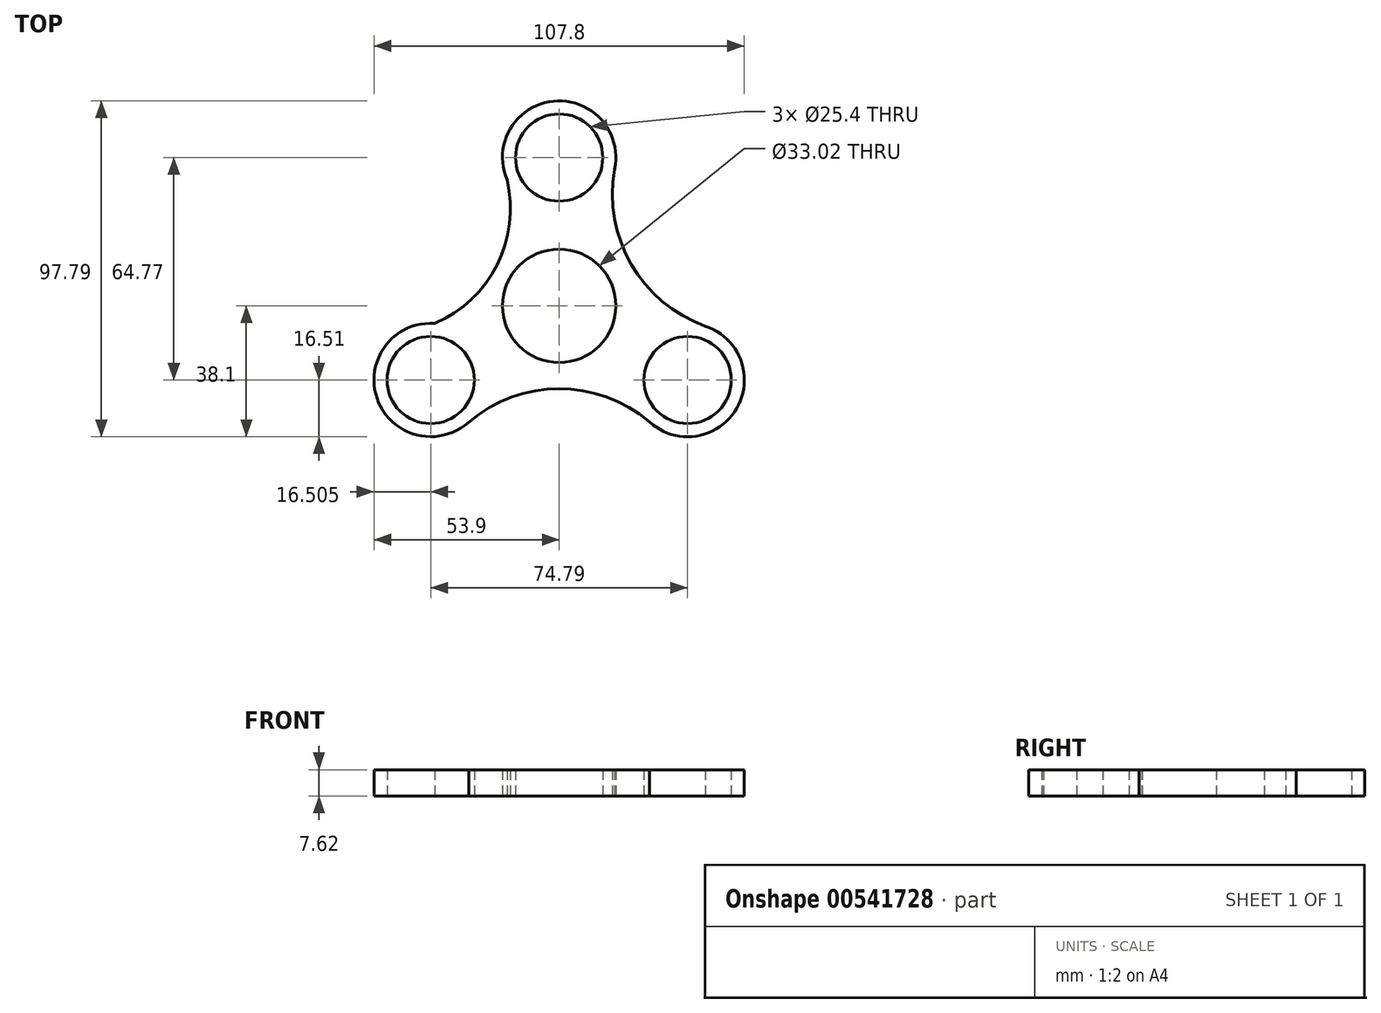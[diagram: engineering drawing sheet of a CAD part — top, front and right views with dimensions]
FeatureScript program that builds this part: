
annotation { "Feature Type Name" : "Feature", "Feature Type Description" : "" }
export const myFeature = defineFeature(function(context is Context, id is Id, definition is map)
    precondition{}
    {
        {
            var Q0;
            Q0=qCreatedBy(makeId("Top.planeOp"),FACE);
            var sketch = newSketch(context, id + "F0", { "sketchPlane" : qUnion([Q0])});
            skCircle(sketch, "E0", {"center": v(0, 0) * mm, "radius": 12.7 * mm});
            skLineSegment(sketch, "E1", {"start": v(0, 0) * mm, "end": v(0, 43.18) * mm});
            skLineSegment(sketch, "E2", {"start": v(0, 0) * mm, "end": v(71.44, 0) * mm});
            skLineSegment(sketch, "E3", {"start": v(0, 0) * mm, "end": v(0, -57.2) * mm});
            skLineSegment(sketch, "E4", {"start": v(0, 0) * mm, "end": v(-62.42, 0) * mm});
            skCircle(sketch, "E5", {"center": v(0, 43.18) * mm, "radius": 12.7 * mm});
            skCircle(sketch, "E6.1.0", {"center": v(-37.4, -21.6) * mm, "radius": 12.7 * mm});
            skCircle(sketch, "E6.2.0", {"center": v(37.4, -21.6) * mm, "radius": 12.7 * mm});
            skCircle(sketch, "E7.0", {"center": v(0, 0) * mm, "radius": 16.51 * mm});
            skCircle(sketch, "E8.0", {"center": v(-37.4, -21.6) * mm, "radius": 16.51 * mm});
            skCircle(sketch, "E9.0", {"center": v(37.4, -21.6) * mm, "radius": 16.51 * mm});
            skCircle(sketch, "E10.0", {"center": v(0, 43.18) * mm, "radius": 16.51 * mm});
            skArc(sketch, "E11", {"start": v(-29.1, -7.32) * mm, "mid": v(-14.57, 8.34) * mm, "end": v(-7.65, 28.55) * mm});
            skArc(sketch, "E12", {"start": v(8.25, 28.88) * mm, "mid": v(14.8, 8.55) * mm, "end": v(29.14, -7.3) * mm});
            skArc(sketch, "E13", {"start": v(20.88, -21.6) * mm, "mid": v(0, -16.81) * mm, "end": v(-20.88, -21.6) * mm});
            skPoint(sketch, "E14", {"position": v(-17.12, 13.53) * mm});
            skPoint(sketch, "E15.end.orphan", {"position": v(-18.7, 10.8) * mm});
            skArc(sketch, "E16", {"start": v(-43.17, -6.12) * mm, "mid": v(-43.08, -6.72) * mm, "end": v(-42.98, -7.32) * mm});
            skArc(sketch, "E17", {"start": v(-42.98, -7.32) * mm, "mid": v(-18.84, 10.53) * mm, "end": v(-16.28, 40.45) * mm});
            skArc(sketch, "E18", {"start": v(16.28, 40.45) * mm, "mid": v(20.99, 12.12) * mm, "end": v(43.17, -6.12) * mm});
            skArc(sketch, "E19", {"start": v(26.89, -34.33) * mm, "mid": v(0.35, -24.16) * mm, "end": v(-26.36, -33.87) * mm});
            skSolve(sketch);
        }
        {
            var Q0;
            Q0 = qSketchRegion(id + "F0", true);
            extrude(context, id + "F1", {"entities" : qUnion([Q0]), "depth" : 7.62 * mm, "offsetDistance" : 25.4 * mm});
        }
        {
            var Q0;
            {var subQ0=sQuery(id+"F0.wireOp",EDGE,"E7.0");var subQ1=sQuery(id+"F0.wireOp",EDGE,"E3");var subQ2=makeQuery(id+"F0.imprint","INTERSECT",VERTEX,{"derivedFrom":[subQ1,subQ0]});Q0=makeQuery(id+"F0.imprint","IMPRINT",FACE,{"disambiguationData":[TD([[makeQuery(id+"F0.imprint","IMPRINT",EDGE,{"disambiguationData":[TD([[subQ2,-1.0]])],"derivedFrom":subQ1}),-1.0]])]});}
            var Q1;
            {var subQ0=sQuery(id+"F0.wireOp",EDGE,"E7.0");var subQ1=sQuery(id+"F0.wireOp",EDGE,"E2");var subQ2=makeQuery(id+"F0.imprint","INTERSECT",VERTEX,{"derivedFrom":[subQ1,subQ0]});Q1=makeQuery(id+"F0.imprint","IMPRINT",FACE,{"disambiguationData":[TD([[makeQuery(id+"F0.imprint","IMPRINT",EDGE,{"disambiguationData":[TD([[subQ2,-1.0]])],"derivedFrom":subQ1}),-1.0]])]});}
            var Q2;
            {var subQ1=sQuery(id+"F0.wireOp",EDGE,"E10.0");var subQ3=sQuery(id+"F0.wireOp",EDGE,"E1");var subQ4=makeQuery(id+"F0.imprint","INTERSECT",VERTEX,{"derivedFrom":[subQ3,subQ1]});Q2=makeQuery(id+"F0.imprint","IMPRINT",FACE,{"disambiguationData":[TD([[makeQuery(id+"F0.imprint","IMPRINT",EDGE,{"disambiguationData":[TD([[subQ4,1.0]])],"derivedFrom":subQ3}),-1.0]])]});}
            var Q3;
            {var subQ1=sQuery(id+"F0.wireOp",EDGE,"E10.0");var subQ3=sQuery(id+"F0.wireOp",EDGE,"E1");var subQ4=makeQuery(id+"F0.imprint","INTERSECT",VERTEX,{"derivedFrom":[subQ3,subQ1]});Q3=makeQuery(id+"F0.imprint","IMPRINT",FACE,{"disambiguationData":[TD([[makeQuery(id+"F0.imprint","IMPRINT",EDGE,{"disambiguationData":[TD([[subQ4,1.0]])],"derivedFrom":subQ3}),1.0]])]});}
            extrude(context, id + "F2", {"entities" : qUnion([Q0, Q1, Q2, Q3]), "operationType" : NewBodyOperationType.ADD, "depth" : 7.62 * mm, "offsetDistance" : 25.4 * mm});
        }
    });
